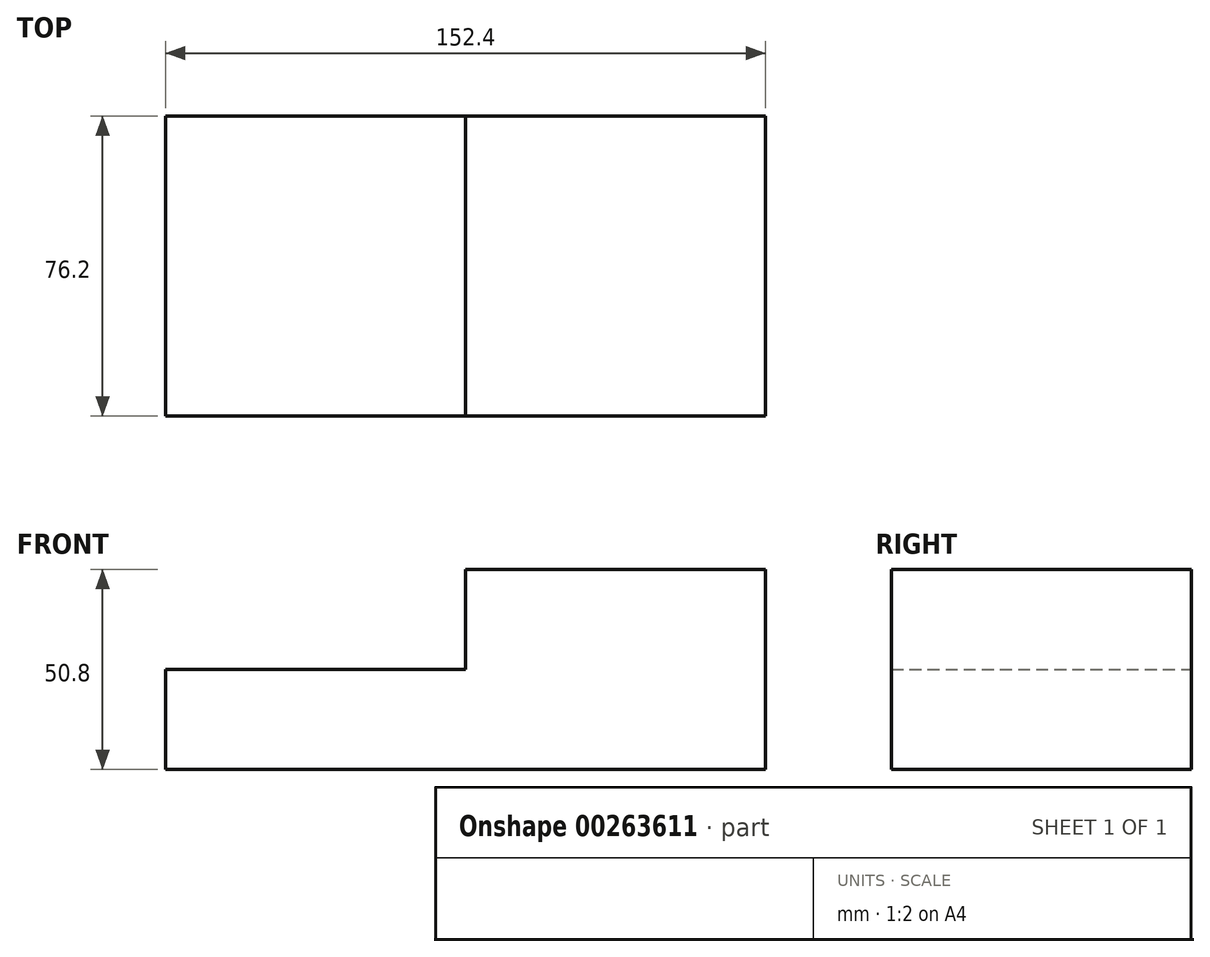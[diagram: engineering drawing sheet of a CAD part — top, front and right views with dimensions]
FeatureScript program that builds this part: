
annotation { "Feature Type Name" : "Feature", "Feature Type Description" : "" }
export const myFeature = defineFeature(function(context is Context, id is Id, definition is map)
    precondition{}
    {
        {
            var Q0;
            Q0=qCreatedBy(makeId("Front.planeOp"),FACE);
            var sketch = newSketch(context, id + "F0", { "sketchPlane" : qUnion([Q0])});
            skLineSegment(sketch, "E0", {"start": v(0, 0) * mm, "end": v(-152.4, 0) * mm});
            skLineSegment(sketch, "E1", {"start": v(0, 0) * mm, "end": v(0, 50.8) * mm});
            skLineSegment(sketch, "E2", {"start": v(0, 50.8) * mm, "end": v(-76.2, 50.8) * mm});
            skLineSegment(sketch, "E3", {"start": v(-76.2, 50.8) * mm, "end": v(-76.2, 25.4) * mm});
            skLineSegment(sketch, "E4", {"start": v(-76.2, 25.4) * mm, "end": v(-152.4, 25.4) * mm});
            skLineSegment(sketch, "E5", {"start": v(-152.4, 25.4) * mm, "end": v(-152.4, 0) * mm});
            skSolve(sketch);
        }
        {
            var Q0;
            Q0=makeQuery(id+"F0.imprint","IMPRINT",FACE,{"disambiguationData":[TD([[makeQuery(id+"F0.imprint","IMPRINT",EDGE,{"derivedFrom":sQuery(id+"F0.wireOp",EDGE,"E0")}),-1.0]])]});
            extrude(context, id + "F1", {"entities" : qUnion([Q0]), "depth" : 76.2 * mm});
        }
    });
